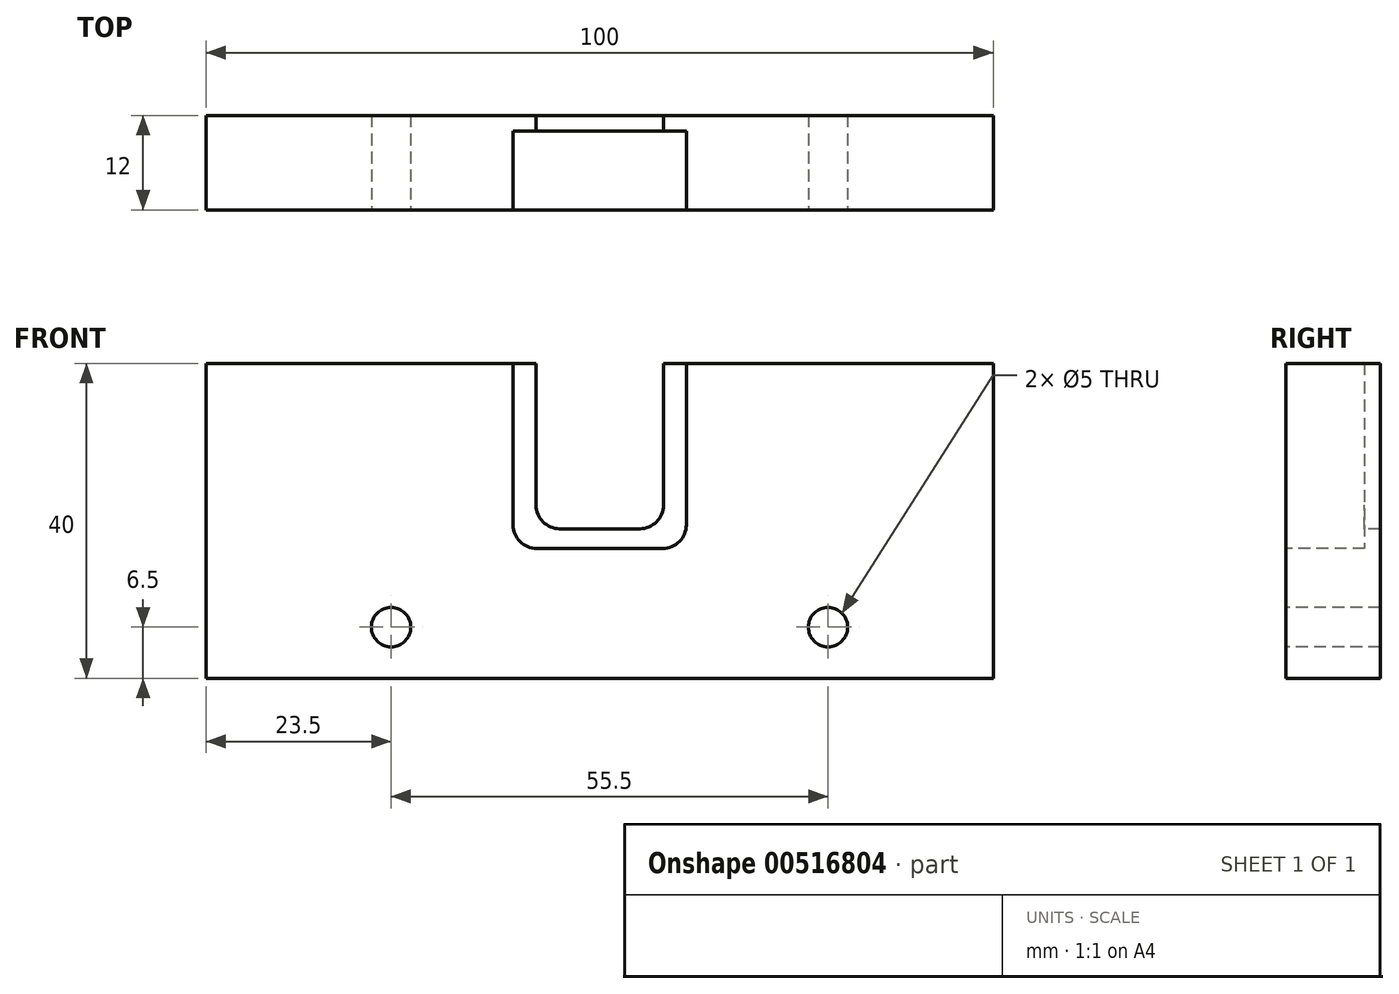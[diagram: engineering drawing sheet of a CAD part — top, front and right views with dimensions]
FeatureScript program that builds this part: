
annotation { "Feature Type Name" : "Feature", "Feature Type Description" : "" }
export const myFeature = defineFeature(function(context is Context, id is Id, definition is map)
    precondition{}
    {
        {
            var Q0;
            Q0=qCreatedBy(makeId("Top.planeOp"),FACE);
            var sketch = newSketch(context, id + "F0", { "sketchPlane" : qUnion([Q0])});
            skLineSegment(sketch, "E0.bottom", {"start": v(0, 0) * mm, "end": v(100, 0) * mm});
            skLineSegment(sketch, "E0.top", {"start": v(0, -12) * mm, "end": v(100, -12) * mm});
            skLineSegment(sketch, "E0.left", {"start": v(0, 0) * mm, "end": v(0, -12) * mm});
            skLineSegment(sketch, "E0.right", {"start": v(100, 0) * mm, "end": v(100, -12) * mm});
            skSolve(sketch);
        }
        {
            var Q0;
            Q0=makeQuery(id+"F0.imprint","IMPRINT",FACE,{"disambiguationData":[TD([[makeQuery(id+"F0.imprint","IMPRINT",EDGE,{"derivedFrom":sQuery(id+"F0.wireOp",EDGE,"E0.bottom")}),-1.0]])]});
            extrude(context, id + "F1", {"entities" : qUnion([Q0]), "depth" : 40 * mm, "offsetDistance" : 25 * mm});
        }
        {
            var Q0;
            Q0=makeQuery(id+"F1.opExtrude","SWEPT_FACE",FACE,{"disambiguationData":[OSD([sQuery(id+"F0.wireOp",EDGE,"E0.top")])]});
            var sketch = newSketch(context, id + "F2", { "sketchPlane" : qUnion([Q0])});
            skCircle(sketch, "E1", {"center": v(23.5, 6.5) * mm, "radius": 2.5 * mm});
            skCircle(sketch, "E2", {"center": v(79, 6.5) * mm, "radius": 2.5 * mm});
            skSolve(sketch);
        }
        {
            var Q0;
            Q0=makeQuery(id+"F2.imprint","IMPRINT",FACE,{"disambiguationData":[TD([[makeQuery(id+"F2.imprint","IMPRINT",EDGE,{"derivedFrom":sQuery(id+"F2.wireOp",EDGE,"E2")}),1.0]])]});
            var Q1;
            Q1=makeQuery(id+"F2.imprint","IMPRINT",FACE,{"disambiguationData":[TD([[makeQuery(id+"F2.imprint","IMPRINT",EDGE,{"derivedFrom":sQuery(id+"F2.wireOp",EDGE,"E1")}),1.0]])]});
            extrude(context, id + "F3", {"entities" : qUnion([Q0, Q1]), "operationType" : NewBodyOperationType.REMOVE, "oppositeDirection" : true, "depth" : 25 * mm, "offsetDistance" : 25 * mm});
        }
        {
            var Q0;
            Q0=makeQuery(id+"F1.opExtrude","SWEPT_FACE",FACE,{"disambiguationData":[OSD([sQuery(id+"F0.wireOp",EDGE,"E0.top")])]});
            var sketch = newSketch(context, id + "F4", { "sketchPlane" : qUnion([Q0])});
            skLineSegment(sketch, "E3", {"start": v(50, 57.12) * mm, "end": v(50, -20.33) * mm, "construction": true});
            skLineSegment(sketch, "E4.bottom", {"start": v(39, 40) * mm, "end": v(61, 40) * mm});
            skLineSegment(sketch, "E4.top", {"start": v(42, 16.5) * mm, "end": v(58, 16.5) * mm});
            skLineSegment(sketch, "E4.left", {"start": v(39, 40) * mm, "end": v(39, 19.5) * mm});
            skLineSegment(sketch, "E4.right", {"start": v(61, 40) * mm, "end": v(61, 19.5) * mm});
            skPoint(sketch, "E5.visualSharp", {"position": v(39, 16.5) * mm});
            skArc(sketch, "E5.filletArc", {"start": v(39, 19.5) * mm, "mid": v(39.88, 17.38) * mm, "end": v(42, 16.5) * mm});
            skPoint(sketch, "E6.visualSharp", {"position": v(61, 16.5) * mm});
            skArc(sketch, "E6.filletArc", {"start": v(58, 16.5) * mm, "mid": v(60.12, 17.38) * mm, "end": v(61, 19.5) * mm});
            skSolve(sketch);
        }
        {
            var Q0;
            Q0=makeQuery(id+"F4.imprint","IMPRINT",FACE,{"disambiguationData":[TD([[makeQuery(id+"F4.imprint","IMPRINT",EDGE,{"derivedFrom":sQuery(id+"F4.wireOp",EDGE,"E4.bottom")}),-1.0]])]});
            extrude(context, id + "F5", {"entities" : qUnion([Q0]), "operationType" : NewBodyOperationType.REMOVE, "oppositeDirection" : true, "depth" : 10 * mm, "offsetDistance" : 25 * mm});
        }
        {
            var Q0;
            Q0=makeQuery(id+"F5.boolean.opBoolean","COPY",FACE,{"derivedFrom":makeQuery(id+"F5.opExtrude","CAP_FACE",FACE,{"disambiguationData":[OSD([sQuery(id+"F4.wireOp",EDGE,"E4.bottom"),sQuery(id+"F4.wireOp",EDGE,"E4.top"),sQuery(id+"F4.wireOp",EDGE,"E4.left"),sQuery(id+"F4.wireOp",EDGE,"E4.right"),sQuery(id+"F4.wireOp",EDGE,"E5.filletArc"),sQuery(id+"F4.wireOp",EDGE,"E6.filletArc")])],"isStart":false})});
            var sketch = newSketch(context, id + "F6", { "sketchPlane" : qUnion([Q0])});
            skLineSegment(sketch, "E7.bottom", {"start": v(41.9, 40) * mm, "end": v(58.1, 40) * mm});
            skLineSegment(sketch, "E7.top", {"start": v(44.9, 19) * mm, "end": v(55.1, 19) * mm});
            skLineSegment(sketch, "E7.left", {"start": v(41.9, 40) * mm, "end": v(41.9, 22) * mm});
            skLineSegment(sketch, "E7.right", {"start": v(58.1, 40) * mm, "end": v(58.1, 22) * mm});
            skPoint(sketch, "E8.visualSharp", {"position": v(41.9, 19) * mm});
            skArc(sketch, "E8.filletArc", {"start": v(41.9, 22) * mm, "mid": v(42.78, 19.88) * mm, "end": v(44.9, 19) * mm});
            skPoint(sketch, "E9.visualSharp", {"position": v(58.1, 19) * mm});
            skArc(sketch, "E9.filletArc", {"start": v(55.1, 19) * mm, "mid": v(57.22, 19.88) * mm, "end": v(58.1, 22) * mm});
            skLineSegment(sketch, "E10", {"start": v(50, 59.1) * mm, "end": v(50, -19.02) * mm, "construction": true});
            skSolve(sketch);
        }
        {
            var Q0;
            Q0 = qSketchRegion(id + "F6", true);
            extrude(context, id + "F7", {"entities" : qUnion([Q0]), "operationType" : NewBodyOperationType.REMOVE, "oppositeDirection" : true, "depth" : 25 * mm, "offsetDistance" : 25 * mm});
        }
    });
